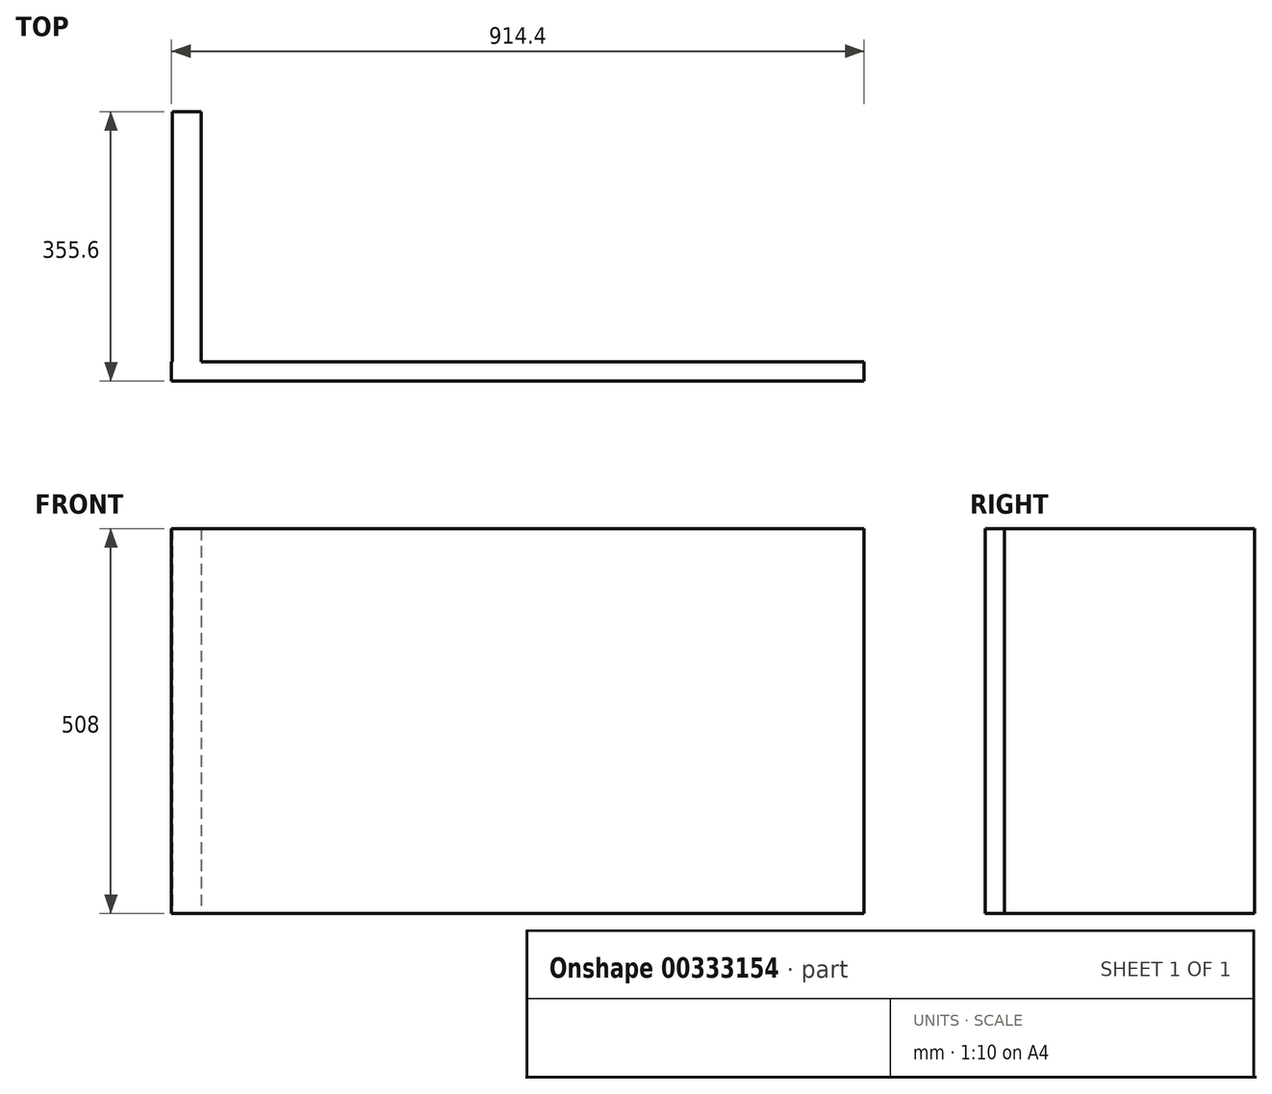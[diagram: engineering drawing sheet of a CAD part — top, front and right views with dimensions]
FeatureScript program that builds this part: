
annotation { "Feature Type Name" : "Feature", "Feature Type Description" : "" }
export const myFeature = defineFeature(function(context is Context, id is Id, definition is map)
    precondition{}
    {
        {
            var Q0;
            Q0=qCreatedBy(makeId("Front.planeOp"),FACE);
            var sketch = newSketch(context, id + "F0", { "sketchPlane" : qUnion([Q0])});
            skLineSegment(sketch, "E0.bottom", {"start": v(-457.2, -254) * mm, "end": v(457.2, -254) * mm});
            skLineSegment(sketch, "E0.top", {"start": v(-457.2, 254) * mm, "end": v(457.2, 254) * mm});
            skLineSegment(sketch, "E0.left", {"start": v(-457.2, -254) * mm, "end": v(-457.2, 254) * mm});
            skLineSegment(sketch, "E0.right", {"start": v(457.2, -254) * mm, "end": v(457.2, 254) * mm});
            skPoint(sketch, "E0.middle", {"position": v(0, 0) * mm});
            skSolve(sketch);
        }
        {
            var Q0;
            Q0 = qSketchRegion(id + "F0", true);
            extrude(context, id + "F1", {"entities" : qUnion([Q0]), "depth" : 25.4 * mm});
        }
        {
            var Q0;
            Q0=qCreatedBy(makeId("Top.planeOp"),FACE);
            var sketch = newSketch(context, id + "F2", { "sketchPlane" : qUnion([Q0])});
            skLineSegment(sketch, "E1.bottom", {"start": v(-455.88, 0) * mm, "end": v(-417.78, 0) * mm});
            skLineSegment(sketch, "E1.top", {"start": v(-455.88, 330.2) * mm, "end": v(-417.78, 330.2) * mm});
            skLineSegment(sketch, "E1.left", {"start": v(-455.88, 0) * mm, "end": v(-455.88, 330.2) * mm});
            skLineSegment(sketch, "E1.right", {"start": v(-417.78, 0) * mm, "end": v(-417.78, 330.2) * mm});
            skSolve(sketch);
        }
        {
            var Q0;
            Q0 = qSketchRegion(id + "F2", true);
            extrude(context, id + "F3", {"entities" : qUnion([Q0]), "operationType" : NewBodyOperationType.ADD, "endBound" : BoundingType.SYMMETRIC, "depth" : 508 * mm});
        }
    });
